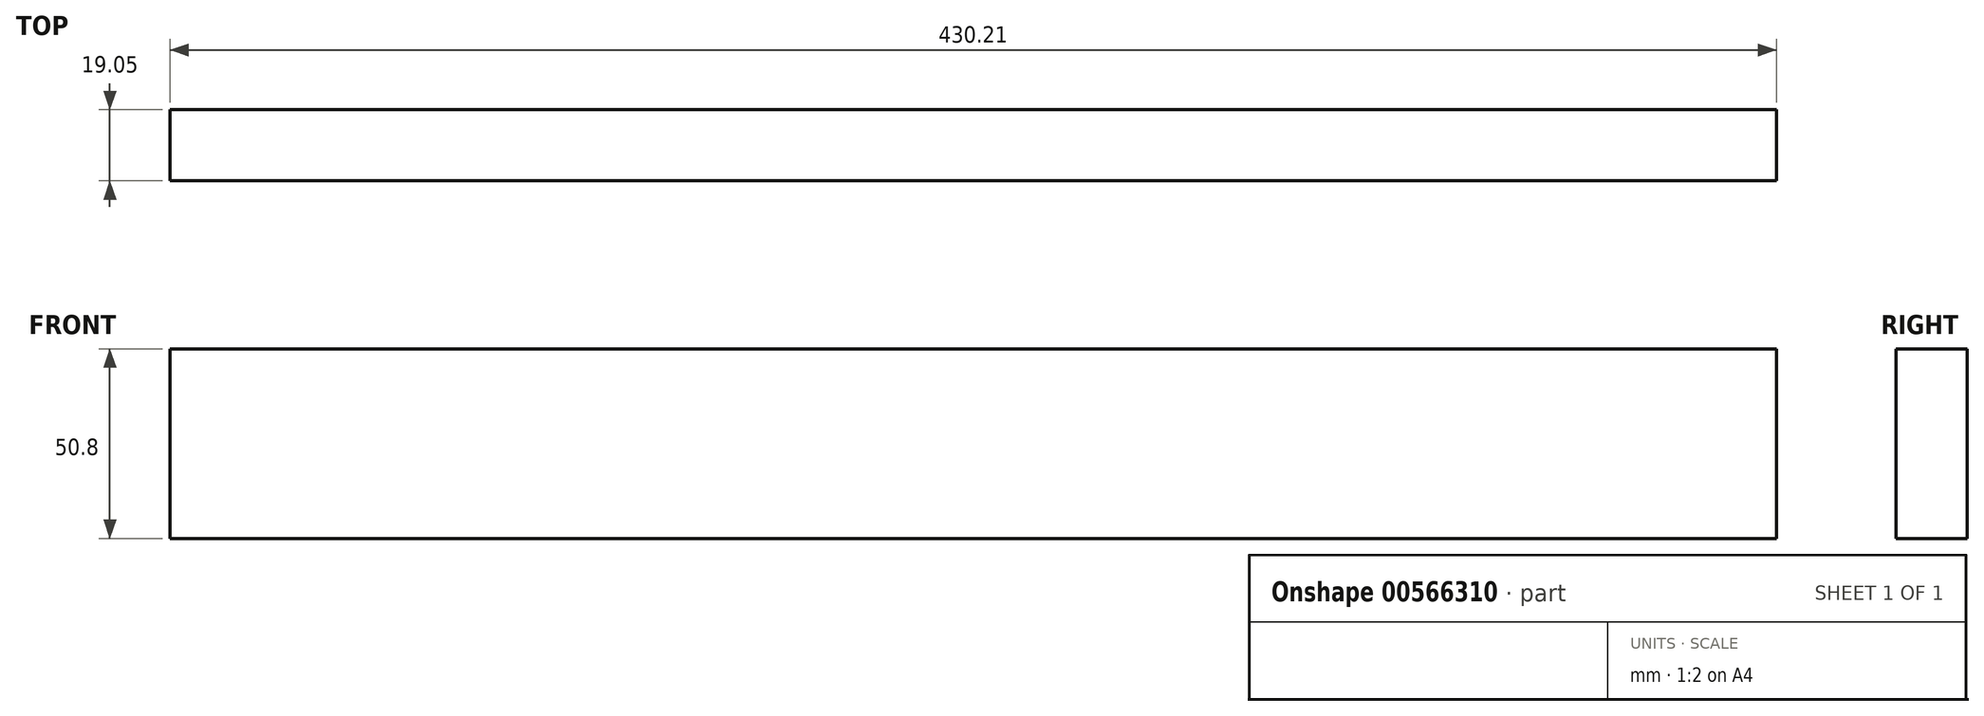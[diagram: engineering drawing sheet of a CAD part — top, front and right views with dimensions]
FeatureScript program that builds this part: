
annotation { "Feature Type Name" : "Feature", "Feature Type Description" : "" }
export const myFeature = defineFeature(function(context is Context, id is Id, definition is map)
    precondition{}
    {
        {
            var Q0;
            Q0=qCreatedBy(makeId("Front.planeOp"),FACE);
            var sketch = newSketch(context, id + "F0", { "sketchPlane" : qUnion([Q0])});
            skLineSegment(sketch, "E0.bottom", {"start": v(0, 0) * mm, "end": v(430.21, 0) * mm});
            skLineSegment(sketch, "E0.top", {"start": v(0, 50.8) * mm, "end": v(430.21, 50.8) * mm});
            skLineSegment(sketch, "E0.left", {"start": v(0, 0) * mm, "end": v(0, 50.8) * mm});
            skLineSegment(sketch, "E0.right", {"start": v(430.21, 0) * mm, "end": v(430.21, 50.8) * mm});
            skSolve(sketch);
        }
        {
            var Q0;
            Q0=makeQuery(id+"F0.imprint","IMPRINT",FACE,{"disambiguationData":[TD([[makeQuery(id+"F0.imprint","IMPRINT",EDGE,{"derivedFrom":sQuery(id+"F0.wireOp",EDGE,"E0.bottom")}),1.0]])]});
            extrude(context, id + "F1", {"entities" : qUnion([Q0]), "depth" : 19.05 * mm, "offsetDistance" : 25.4 * mm});
        }
    });
